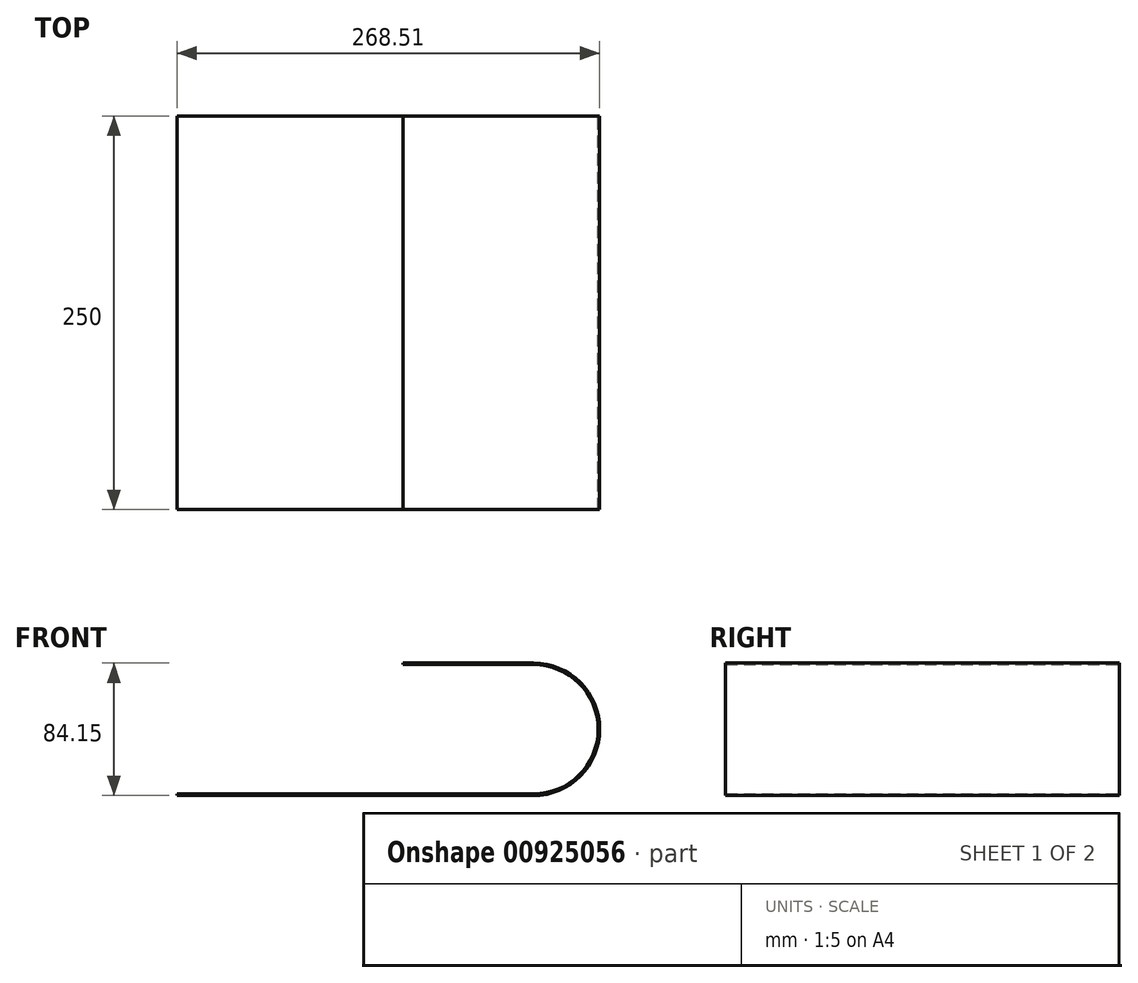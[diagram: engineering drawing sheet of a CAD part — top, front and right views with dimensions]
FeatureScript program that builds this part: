
annotation { "Feature Type Name" : "Feature", "Feature Type Description" : "" }
export const myFeature = defineFeature(function(context is Context, id is Id, definition is map)
    precondition{}
    {
        {
            var Q0;
            Q0=qCreatedBy(makeId("Front.planeOp"),FACE);
            var sketch = newSketch(context, id + "F0", { "sketchPlane" : qUnion([Q0])});
            skLineSegment(sketch, "E0", {"start": v(-75.8, 0) * mm, "end": v(150.62, 0) * mm});
            skArc(sketch, "E1", {"start": v(150.62, 0) * mm, "mid": v(191.7, 41.08) * mm, "end": v(150.62, 82.15) * mm});
            skLineSegment(sketch, "E2", {"start": v(150.62, 82.15) * mm, "end": v(92.92, 82.15) * mm});
            skLineSegment(sketch, "E3.0", {"start": v(150.62, 83.15) * mm, "end": v(92.92, 83.15) * mm});
            skArc(sketch, "E3.1", {"start": v(150.62, -1) * mm, "mid": v(192.7, 41.08) * mm, "end": v(150.62, 83.15) * mm});
            skLineSegment(sketch, "E3.2", {"start": v(-75.8, -1) * mm, "end": v(150.62, -1) * mm});
            skLineSegment(sketch, "E4", {"start": v(92.92, 83.15) * mm, "end": v(92.92, 82.15) * mm});
            skLineSegment(sketch, "E5", {"start": v(-75.8, 0) * mm, "end": v(-75.8, -1) * mm});
            skSolve(sketch);
        }
        {
            var Q0;
            Q0=makeQuery(id+"F0.imprint","IMPRINT",FACE,{"disambiguationData":[TD([[makeQuery(id+"F0.imprint","IMPRINT",EDGE,{"derivedFrom":sQuery(id+"F0.wireOp",EDGE,"E0")}),-1.0]])]});
            extrude(context, id + "F1", {"entities" : qUnion([Q0]), "depth" : 250 * mm, "offsetDistance" : 25 * mm});
        }
        {
            var Q0;
            Q0=makeQuery(id+"F1.opExtrude","SWEPT_FACE",FACE,{"disambiguationData":[OSD([sQuery(id+"F0.wireOp",EDGE,"E4")])]});
            extrude(context, id + "F2", {"entities" : qUnion([Q0]), "operationType" : NewBodyOperationType.ADD, "depth" : 25 * mm, "offsetDistance" : 25 * mm});
        }
    });
